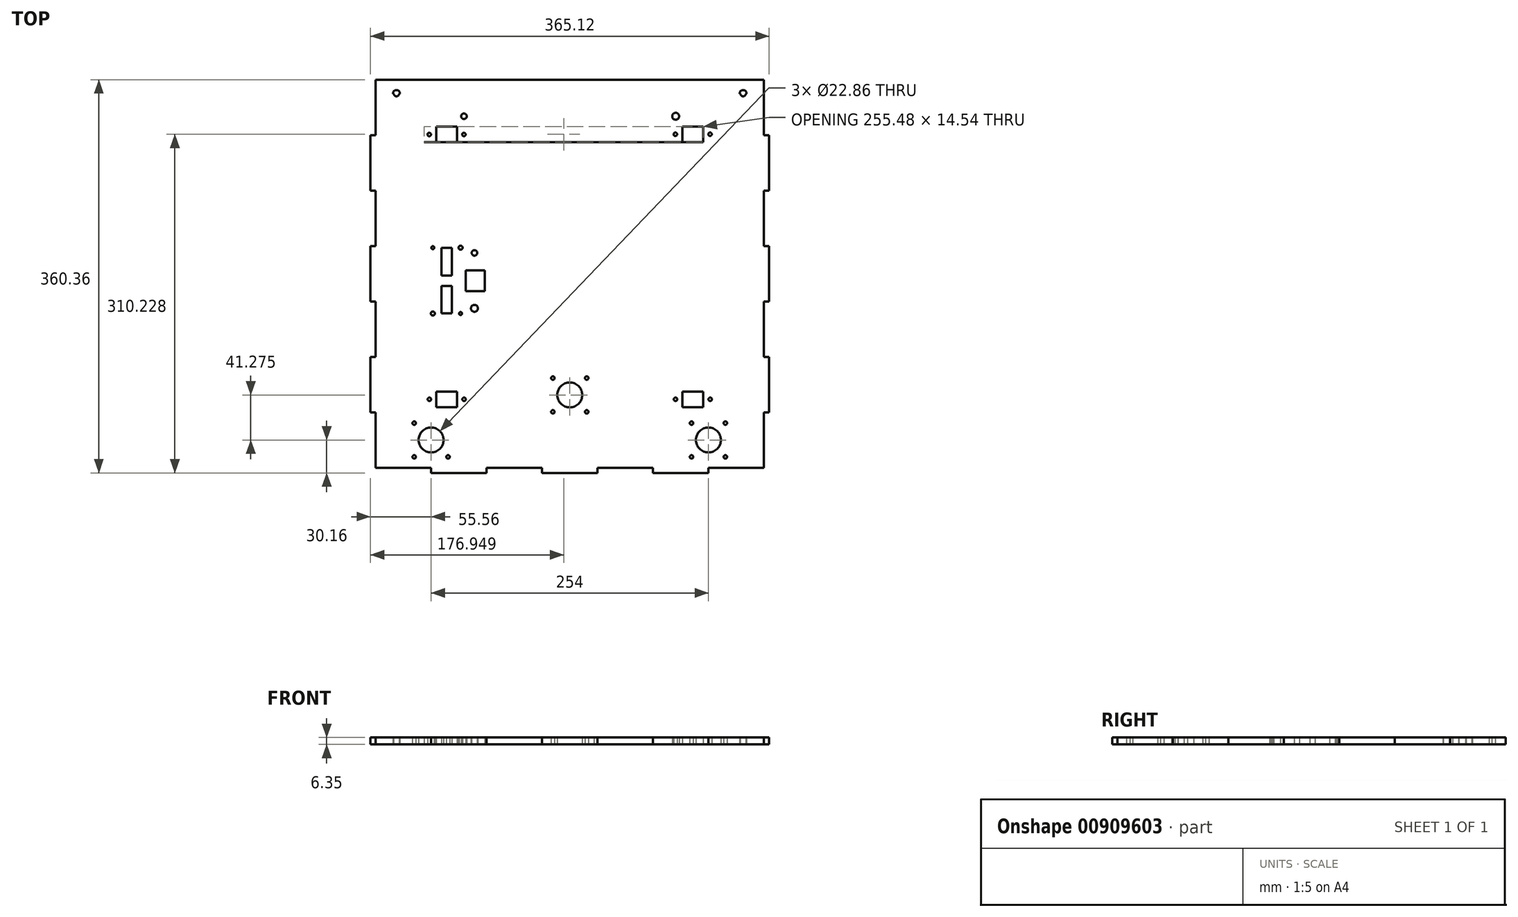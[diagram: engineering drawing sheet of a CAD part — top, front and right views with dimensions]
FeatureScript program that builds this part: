
annotation { "Feature Type Name" : "Feature", "Feature Type Description" : "" }
export const myFeature = defineFeature(function(context is Context, id is Id, definition is map)
    precondition{}
    {
        {
            var Q0;
            Q0=qCreatedBy(makeId("Top.planeOp"),FACE);
            var sketch = newSketch(context, id + "F0", { "sketchPlane" : qUnion([Q0])});
            skLineSegment(sketch, "E0.bottom", {"start": v(-177.8, 171.45) * mm, "end": v(177.8, 171.45) * mm});
            skLineSegment(sketch, "E0.top", {"start": v(-177.8, -171.45) * mm, "end": v(177.8, -171.45) * mm});
            skLineSegment(sketch, "E0.left", {"start": v(-177.8, 171.45) * mm, "end": v(-177.8, -171.45) * mm});
            skLineSegment(sketch, "E0.right", {"start": v(177.8, 171.45) * mm, "end": v(177.8, -171.45) * mm});
            skPoint(sketch, "E0.middle", {"position": v(0, 0) * mm});
            skLineSegment(sketch, "E1.0", {"start": v(-133.35, -101.6) * mm, "end": v(133.35, -101.6) * mm});
            skLineSegment(sketch, "E2.0", {"start": v(-133.35, 127) * mm, "end": v(-133.35, -101.6) * mm});
            skLineSegment(sketch, "E3", {"start": v(0, 171.45) * mm, "end": v(0, -171.45) * mm, "construction": true});
            skLineSegment(sketch, "E4", {"start": v(-177.8, 0) * mm, "end": v(177.8, 0) * mm, "construction": true});
            skLineSegment(sketch, "E5.MirrorCS", {"start": v(133.35, 127) * mm, "end": v(133.35, -101.6) * mm});
            skLineSegment(sketch, "E6.0", {"start": v(-133.35, 127) * mm, "end": v(133.35, 127) * mm});
            skLineSegment(sketch, "E7.bottom", {"start": v(-130.17, 34.93) * mm, "end": v(-95.25, 34.93) * mm});
            skLineSegment(sketch, "E7.top", {"start": v(-130.17, -34.92) * mm, "end": v(-95.25, -34.92) * mm});
            skLineSegment(sketch, "E7.left", {"start": v(-130.18, 34.92) * mm, "end": v(-130.18, -34.92) * mm});
            skLineSegment(sketch, "E7.right", {"start": v(-95.25, 34.92) * mm, "end": v(-95.25, -34.92) * mm});
            skLineSegment(sketch, "E8", {"start": v(-112.71, 34.93) * mm, "end": v(-112.71, -171.45) * mm, "construction": true});
            skLineSegment(sketch, "E9.bottom", {"start": v(-107.95, 4.76) * mm, "end": v(-117.48, 4.76) * mm});
            skLineSegment(sketch, "E9.top", {"start": v(-107.95, 30.04) * mm, "end": v(-117.48, 30.04) * mm});
            skLineSegment(sketch, "E9.left", {"start": v(-107.95, 4.76) * mm, "end": v(-107.95, 30.04) * mm});
            skLineSegment(sketch, "E9.right", {"start": v(-117.48, 4.76) * mm, "end": v(-117.48, 30.04) * mm});
            skPoint(sketch, "E10", {"position": v(-95.25, 0) * mm});
            skLineSegment(sketch, "E11.MirrorCS", {"start": v(-117.48, -4.76) * mm, "end": v(-117.48, -30.04) * mm});
            skLineSegment(sketch, "E12.MirrorCS", {"start": v(-107.95, -4.76) * mm, "end": v(-107.95, -30.04) * mm});
            skPoint(sketch, "E13.MirrorP", {"position": v(-112.71, -12.57) * mm});
            skLineSegment(sketch, "E14.MirrorCS", {"start": v(-107.95, -4.76) * mm, "end": v(-117.48, -4.76) * mm});
            skLineSegment(sketch, "E15.MirrorCS", {"start": v(-107.95, -30.04) * mm, "end": v(-117.48, -30.04) * mm});
            skCircle(sketch, "E16", {"center": v(-127, -146.05) * mm, "radius": 11.43 * mm});
            skCircle(sketch, "E17", {"center": v(-111.5, -130.56) * mm, "radius": 1.59 * mm});
            skCircle(sketch, "E18.1.0", {"center": v(-142.5, -130.56) * mm, "radius": 1.59 * mm});
            skCircle(sketch, "E18.2.0", {"center": v(-142.5, -161.54) * mm, "radius": 1.59 * mm});
            skCircle(sketch, "E18.3.0", {"center": v(-111.5, -161.54) * mm, "radius": 1.59 * mm});
            skCircle(sketch, "E19.MirrorC", {"center": v(142.5, -130.56) * mm, "radius": 1.59 * mm});
            skCircle(sketch, "E20.MirrorC", {"center": v(111.5, -130.56) * mm, "radius": 1.59 * mm});
            skCircle(sketch, "E21.MirrorC", {"center": v(142.5, -161.54) * mm, "radius": 1.59 * mm});
            skPoint(sketch, "E22.MirrorP", {"position": v(127, -146.05) * mm});
            skCircle(sketch, "E23.MirrorC", {"center": v(111.5, -161.54) * mm, "radius": 1.59 * mm});
            skCircle(sketch, "E24.MirrorC", {"center": v(127, -146.05) * mm, "radius": 11.43 * mm});
            skPoint(sketch, "E25.orphan", {"position": v(-112.71, -34.93) * mm});
            skCircle(sketch, "E26", {"center": v(-128.59, -108.75) * mm, "radius": 1.59 * mm});
            skCircle(sketch, "E27.MirrorC", {"center": v(-96.84, -108.75) * mm, "radius": 1.59 * mm});
            skLineSegment(sketch, "E28.bottom", {"start": v(-122.24, -101.6) * mm, "end": v(-103.19, -101.6) * mm});
            skLineSegment(sketch, "E28.top", {"start": v(-122.24, -115.9) * mm, "end": v(-103.19, -115.9) * mm});
            skLineSegment(sketch, "E28.left", {"start": v(-122.24, -101.6) * mm, "end": v(-122.24, -115.9) * mm});
            skLineSegment(sketch, "E28.right", {"start": v(-103.19, -101.6) * mm, "end": v(-103.19, -115.9) * mm});
            skPoint(sketch, "E29", {"position": v(-112.71, -115.9) * mm});
            skLineSegment(sketch, "E30.MirrorCS", {"start": v(122.24, -101.6) * mm, "end": v(122.24, -115.9) * mm});
            skCircle(sketch, "E31.MirrorC", {"center": v(96.84, -108.75) * mm, "radius": 1.59 * mm});
            skCircle(sketch, "E32.MirrorC", {"center": v(128.59, -108.75) * mm, "radius": 1.59 * mm});
            skLineSegment(sketch, "E33.MirrorCS", {"start": v(122.24, -101.6) * mm, "end": v(103.19, -101.6) * mm});
            skPoint(sketch, "E34.MirrorP", {"position": v(112.71, -115.9) * mm});
            skLineSegment(sketch, "E35.MirrorCS", {"start": v(103.19, -101.6) * mm, "end": v(103.19, -115.9) * mm});
            skLineSegment(sketch, "E36.MirrorCS", {"start": v(122.24, -115.9) * mm, "end": v(103.19, -115.9) * mm});
            skCircle(sketch, "E37.MirrorC", {"center": v(-128.7, 133.9) * mm, "radius": 1.59 * mm});
            skLineSegment(sketch, "E38.MirrorCS", {"start": v(-122.36, 141.06) * mm, "end": v(-103.3, 141.07) * mm});
            skLineSegment(sketch, "E39.MirrorCS", {"start": v(-122.35, 126.76) * mm, "end": v(-103.3, 126.77) * mm});
            skCircle(sketch, "E40.MirrorC", {"center": v(128.47, 134.15) * mm, "radius": 1.59 * mm});
            skLineSegment(sketch, "E41.MirrorCS", {"start": v(-122.35, 126.76) * mm, "end": v(-122.36, 141.06) * mm});
            skCircle(sketch, "E42.MirrorC", {"center": v(-96.95, 133.93) * mm, "radius": 1.59 * mm});
            skLineSegment(sketch, "E43.MirrorCS", {"start": v(122.12, 141.29) * mm, "end": v(103.07, 141.27) * mm});
            skCircle(sketch, "E44.MirrorC", {"center": v(96.72, 134.12) * mm, "radius": 1.59 * mm});
            skLineSegment(sketch, "E45.MirrorCS", {"start": v(122.13, 126.99) * mm, "end": v(103.08, 126.97) * mm});
            skPoint(sketch, "E46.MirrorP", {"position": v(-112.83, 141.07) * mm});
            skPoint(sketch, "E47.MirrorP", {"position": v(112.6, 141.28) * mm});
            skLineSegment(sketch, "E48.MirrorCS", {"start": v(-133.46, 126.75) * mm, "end": v(133.24, 127) * mm});
            skLineSegment(sketch, "E49.MirrorCS", {"start": v(103.08, 126.97) * mm, "end": v(103.07, 141.27) * mm});
            skLineSegment(sketch, "E50.MirrorCS", {"start": v(-103.3, 126.77) * mm, "end": v(-103.3, 141.07) * mm});
            skLineSegment(sketch, "E51.MirrorCS", {"start": v(122.13, 126.99) * mm, "end": v(122.12, 141.29) * mm});
            skLineSegment(sketch, "E52.bottom", {"start": v(-95.25, -9.53) * mm, "end": v(-77.79, -9.53) * mm});
            skLineSegment(sketch, "E52.top", {"start": v(-95.25, 9.52) * mm, "end": v(-77.79, 9.52) * mm});
            skLineSegment(sketch, "E52.left", {"start": v(-95.25, -9.53) * mm, "end": v(-95.25, 9.52) * mm});
            skLineSegment(sketch, "E52.right", {"start": v(-77.79, -9.53) * mm, "end": v(-77.79, 9.52) * mm});
            skPoint(sketch, "E53", {"position": v(-65.09, 0) * mm});
            skLineSegment(sketch, "E54.bottom", {"start": v(-95.25, -34.92) * mm, "end": v(-77.79, -34.92) * mm});
            skLineSegment(sketch, "E54.top", {"start": v(-95.25, 34.93) * mm, "end": v(-77.79, 34.93) * mm});
            skLineSegment(sketch, "E54.left", {"start": v(-95.25, -34.92) * mm, "end": v(-95.25, 34.92) * mm});
            skLineSegment(sketch, "E54.right", {"start": v(-77.79, -34.92) * mm, "end": v(-77.79, 34.92) * mm});
            skLineSegment(sketch, "E55.0", {"start": v(-100.01, 34.92) * mm, "end": v(-77.79, 34.92) * mm});
            skLineSegment(sketch, "E55.1", {"start": v(-130.18, 34.92) * mm, "end": v(-100.01, 34.92) * mm});
            skLineSegment(sketch, "E56", {"start": v(-77.79, 34.92) * mm, "end": v(-77.79, 34.92) * mm});
            skLineSegment(sketch, "E57", {"start": v(-130.18, 34.92) * mm, "end": v(-130.18, 34.92) * mm});
            skLineSegment(sketch, "E58.MirrorCS", {"start": v(-130.18, -34.92) * mm, "end": v(-130.18, -34.92) * mm});
            skLineSegment(sketch, "E59.MirrorCS", {"start": v(-100.01, -34.93) * mm, "end": v(-77.79, -34.93) * mm});
            skLineSegment(sketch, "E60.MirrorCS", {"start": v(-130.18, -34.93) * mm, "end": v(-100.01, -34.93) * mm});
            skLineSegment(sketch, "E61.MirrorCS", {"start": v(-77.79, -34.92) * mm, "end": v(-77.79, -34.92) * mm});
            skCircle(sketch, "E62", {"center": v(-87.31, 25.4) * mm, "radius": 3.18 * mm});
            skCircle(sketch, "E63.MirrorC", {"center": v(-87.31, -25.4) * mm, "radius": 3.18 * mm});
            skCircle(sketch, "E64", {"center": v(-125.41, 30.16) * mm, "radius": 1.84 * mm});
            skCircle(sketch, "E65.MirrorC", {"center": v(-100.01, 30.16) * mm, "radius": 1.84 * mm});
            skCircle(sketch, "E66.MirrorC", {"center": v(-125.41, -30.16) * mm, "radius": 1.84 * mm});
            skCircle(sketch, "E67.MirrorC", {"center": v(-100.01, -30.16) * mm, "radius": 1.84 * mm});
            skCircle(sketch, "E68", {"center": v(-158.75, 171.45) * mm, "radius": 3.18 * mm});
            skCircle(sketch, "E69", {"center": v(-96.95, 150.6) * mm, "radius": 3.18 * mm});
            skCircle(sketch, "E70.MirrorC", {"center": v(96.95, 150.6) * mm, "radius": 3.18 * mm});
            skCircle(sketch, "E71.MirrorC", {"center": v(158.75, 171.45) * mm, "radius": 3.18 * mm});
            skLineSegment(sketch, "E72.0", {"start": v(-177.8, 184.15) * mm, "end": v(177.8, 184.15) * mm});
            skLineSegment(sketch, "E73", {"start": v(-177.8, 171.45) * mm, "end": v(-177.8, 184.15) * mm});
            skLineSegment(sketch, "E74", {"start": v(177.8, 171.45) * mm, "end": v(177.8, 184.15) * mm});
            skLineSegment(sketch, "E75.bottom", {"start": v(-177.8, 133.35) * mm, "end": v(-182.56, 133.35) * mm});
            skLineSegment(sketch, "E75.top", {"start": v(-177.8, 82.55) * mm, "end": v(-182.56, 82.55) * mm});
            skLineSegment(sketch, "E75.left", {"start": v(-177.8, 133.35) * mm, "end": v(-177.8, 82.55) * mm});
            skLineSegment(sketch, "E75.right", {"start": v(-182.56, 133.35) * mm, "end": v(-182.56, 82.55) * mm});
            skLineSegment(sketch, "E76.bottom", {"start": v(-177.8, 31.75) * mm, "end": v(-182.56, 31.75) * mm});
            skLineSegment(sketch, "E76.top", {"start": v(-177.8, -19.05) * mm, "end": v(-182.56, -19.05) * mm});
            skLineSegment(sketch, "E76.left", {"start": v(-177.8, 31.75) * mm, "end": v(-177.8, -19.05) * mm});
            skLineSegment(sketch, "E76.right", {"start": v(-182.56, 31.75) * mm, "end": v(-182.56, -19.05) * mm});
            skLineSegment(sketch, "E77.bottom", {"start": v(-177.8, -69.85) * mm, "end": v(-182.56, -69.85) * mm});
            skLineSegment(sketch, "E77.top", {"start": v(-177.8, -120.65) * mm, "end": v(-182.56, -120.65) * mm});
            skLineSegment(sketch, "E77.left", {"start": v(-177.8, -69.85) * mm, "end": v(-177.8, -120.65) * mm});
            skLineSegment(sketch, "E77.right", {"start": v(-182.56, -69.85) * mm, "end": v(-182.56, -120.65) * mm});
            skLineSegment(sketch, "E78.MirrorCS", {"start": v(177.8, -120.65) * mm, "end": v(182.56, -120.65) * mm});
            skLineSegment(sketch, "E79.MirrorCS", {"start": v(177.8, 31.75) * mm, "end": v(182.56, 31.75) * mm});
            skLineSegment(sketch, "E80.MirrorCS", {"start": v(177.8, -19.05) * mm, "end": v(182.56, -19.05) * mm});
            skLineSegment(sketch, "E81.MirrorCS", {"start": v(177.8, 82.55) * mm, "end": v(182.56, 82.55) * mm});
            skLineSegment(sketch, "E82.MirrorCS", {"start": v(177.8, -69.85) * mm, "end": v(182.56, -69.85) * mm});
            skLineSegment(sketch, "E83.MirrorCS", {"start": v(177.8, 133.35) * mm, "end": v(182.56, 133.35) * mm});
            skLineSegment(sketch, "E84.MirrorCS", {"start": v(182.56, 133.35) * mm, "end": v(182.56, 82.55) * mm});
            skLineSegment(sketch, "E85.MirrorCS", {"start": v(177.8, 31.75) * mm, "end": v(177.8, -19.05) * mm});
            skLineSegment(sketch, "E86.MirrorCS", {"start": v(182.56, 31.75) * mm, "end": v(182.56, -19.05) * mm});
            skLineSegment(sketch, "E87.MirrorCS", {"start": v(177.8, 133.35) * mm, "end": v(177.8, 82.55) * mm});
            skLineSegment(sketch, "E88.MirrorCS", {"start": v(177.8, -69.85) * mm, "end": v(177.8, -120.65) * mm});
            skLineSegment(sketch, "E89.MirrorCS", {"start": v(182.56, -69.85) * mm, "end": v(182.56, -120.65) * mm});
            skLineSegment(sketch, "E90.bottom", {"start": v(-127, 184.15) * mm, "end": v(-76.2, 184.15) * mm});
            skLineSegment(sketch, "E90.top", {"start": v(-127, 188.91) * mm, "end": v(-76.2, 188.91) * mm});
            skLineSegment(sketch, "E90.left", {"start": v(-127, 184.15) * mm, "end": v(-127, 188.91) * mm});
            skLineSegment(sketch, "E90.right", {"start": v(-76.2, 184.15) * mm, "end": v(-76.2, 188.91) * mm});
            skLineSegment(sketch, "E91.bottom", {"start": v(-25.4, 184.15) * mm, "end": v(25.4, 184.15) * mm});
            skLineSegment(sketch, "E91.top", {"start": v(-25.4, 188.91) * mm, "end": v(25.4, 188.91) * mm});
            skLineSegment(sketch, "E91.left", {"start": v(-25.4, 184.15) * mm, "end": v(-25.4, 188.91) * mm});
            skLineSegment(sketch, "E91.right", {"start": v(25.4, 184.15) * mm, "end": v(25.4, 188.91) * mm});
            skLineSegment(sketch, "E92.bottom", {"start": v(76.2, 184.15) * mm, "end": v(127, 184.15) * mm});
            skLineSegment(sketch, "E92.top", {"start": v(76.2, 188.91) * mm, "end": v(127, 188.91) * mm});
            skLineSegment(sketch, "E92.left", {"start": v(76.2, 184.15) * mm, "end": v(76.2, 188.91) * mm});
            skLineSegment(sketch, "E92.right", {"start": v(127, 184.15) * mm, "end": v(127, 188.91) * mm});
            skLineSegment(sketch, "E93", {"start": v(177.8, 184.15) * mm, "end": v(177.8, -171.45) * mm, "construction": true});
            skLineSegment(sketch, "E94", {"start": v(177.8, 6.35) * mm, "end": v(-210.69, 6.35) * mm, "construction": true});
            skLineSegment(sketch, "E95.MirrorCS", {"start": v(25.4, -171.45) * mm, "end": v(25.4, -176.21) * mm});
            skLineSegment(sketch, "E96.MirrorCS", {"start": v(76.2, -171.45) * mm, "end": v(76.2, -176.21) * mm});
            skLineSegment(sketch, "E97.MirrorCS", {"start": v(127, -171.45) * mm, "end": v(127, -176.21) * mm});
            skLineSegment(sketch, "E98.MirrorCS", {"start": v(-127, -171.45) * mm, "end": v(-127, -176.21) * mm});
            skLineSegment(sketch, "E99.MirrorCS", {"start": v(-25.4, -171.45) * mm, "end": v(-25.4, -176.21) * mm});
            skLineSegment(sketch, "E100.MirrorCS", {"start": v(-76.2, -171.45) * mm, "end": v(-76.2, -176.21) * mm});
            skLineSegment(sketch, "E101.MirrorCS", {"start": v(76.2, -171.45) * mm, "end": v(127, -171.45) * mm});
            skLineSegment(sketch, "E102.MirrorCS", {"start": v(-127, -176.21) * mm, "end": v(-76.2, -176.21) * mm});
            skLineSegment(sketch, "E103.MirrorCS", {"start": v(76.2, -176.21) * mm, "end": v(127, -176.21) * mm});
            skLineSegment(sketch, "E104.MirrorCS", {"start": v(-25.4, -171.45) * mm, "end": v(25.4, -171.45) * mm});
            skLineSegment(sketch, "E105.MirrorCS", {"start": v(-25.4, -176.21) * mm, "end": v(25.4, -176.21) * mm});
            skLineSegment(sketch, "E106.MirrorCS", {"start": v(-127, -171.45) * mm, "end": v(-76.2, -171.45) * mm});
            skLineSegment(sketch, "E107.bottom", {"start": v(-22.23, 126.85) * mm, "end": v(22.22, 126.85) * mm});
            skLineSegment(sketch, "E107.top", {"start": v(-22.23, 168.13) * mm, "end": v(22.22, 168.13) * mm});
            skLineSegment(sketch, "E107.left", {"start": v(-22.23, 126.85) * mm, "end": v(-22.23, 168.13) * mm});
            skLineSegment(sketch, "E107.right", {"start": v(22.22, 126.85) * mm, "end": v(22.22, 168.13) * mm});
            skPoint(sketch, "E108", {"position": v(0, 168.13) * mm});
            skCircle(sketch, "E109", {"center": v(0, -104.77) * mm, "radius": 11.43 * mm});
            skLineSegment(sketch, "E110.bottom", {"start": v(20.64, -84.14) * mm, "end": v(-20.64, -84.14) * mm});
            skLineSegment(sketch, "E110.top", {"start": v(20.64, -125.41) * mm, "end": v(-20.64, -125.41) * mm});
            skLineSegment(sketch, "E110.left", {"start": v(20.64, -84.14) * mm, "end": v(20.64, -125.41) * mm});
            skLineSegment(sketch, "E110.right", {"start": v(-20.64, -84.14) * mm, "end": v(-20.64, -125.41) * mm});
            skCircle(sketch, "E111", {"center": v(-15.5, -120.27) * mm, "radius": 1.59 * mm});
            skCircle(sketch, "E112.1.0", {"center": v(15.5, -120.27) * mm, "radius": 1.59 * mm});
            skCircle(sketch, "E112.2.0", {"center": v(15.5, -89.28) * mm, "radius": 1.59 * mm});
            skCircle(sketch, "E113.1.3.0", {"center": v(-15.5, -89.28) * mm, "radius": 1.59 * mm});
            skSolve(sketch);
        }
        {
            var Q0;
            Q0=makeQuery(id+"F0.imprint","IMPRINT",FACE,{"disambiguationData":[TD([[makeQuery(id+"F0.imprint","IMPRINT",EDGE,{"derivedFrom":sQuery(id+"F0.wireOp",EDGE,"E0.bottom")}),-1.0]])]});
            var Q1;
            {var subQ0=sQuery(id+"F0.wireOp",EDGE,"E7.bottom");Q1=makeQuery(id+"F0.imprint","IMPRINT",FACE,{"disambiguationData":[TD([[makeQuery(id+"F0.imprint","IMPRINT",EDGE,{"derivedFrom":subQ0}),-1.0]])]});}
            var Q2;
            {var subQ1=sQuery(id+"F0.wireOp",EDGE,"E52.bottom");Q2=makeQuery(id+"F0.imprint","IMPRINT",FACE,{"disambiguationData":[TD([[makeQuery(id+"F0.imprint","IMPRINT",EDGE,{"derivedFrom":subQ1}),-1.0]])]});}
            var Q3;
            {var subQ7=sQuery(id+"F0.wireOp",EDGE,"E52.top");Q3=makeQuery(id+"F0.imprint","IMPRINT",FACE,{"disambiguationData":[TD([[makeQuery(id+"F0.imprint","IMPRINT",EDGE,{"derivedFrom":subQ7}),1.0]])]});}
            var Q4;
            {var subQ0=sQuery(id+"F0.wireOp",EDGE,"E7.top");Q4=makeQuery(id+"F0.imprint","IMPRINT",FACE,{"disambiguationData":[TD([[makeQuery(id+"F0.imprint","IMPRINT",EDGE,{"derivedFrom":subQ0}),-1.0]])]});}
            var Q5;
            {var subQ1=sQuery(id+"F0.wireOp",EDGE,"E7.bottom");Q5=makeQuery(id+"F0.imprint","IMPRINT",FACE,{"disambiguationData":[TD([[makeQuery(id+"F0.imprint","IMPRINT",EDGE,{"derivedFrom":subQ1}),1.0]])]});}
            var Q6;
            {var subQ0=sQuery(id+"F0.wireOp",EDGE,"E62");var subQ1=sQuery(id+"F0.wireOp",EDGE,"E54.top");var subQ2=makeQuery(id+"F0.imprint","INTERSECT",VERTEX,{"disambiguationData":[OD(0.0)],"derivedFrom":[subQ1,subQ0]});Q6=makeQuery(id+"F0.imprint","IMPRINT",FACE,{"disambiguationData":[TD([[makeQuery(id+"F0.imprint","IMPRINT",EDGE,{"disambiguationData":[TD([[subQ2,-1.0]])],"derivedFrom":subQ1}),-1.0]])]});}
            var Q7;
            Q7=makeQuery(id+"F0.imprint","IMPRINT",FACE,{"disambiguationData":[TD([[makeQuery(id+"F0.imprint","IMPRINT",EDGE,{"derivedFrom":sQuery(id+"F0.wireOp",EDGE,"E65.MirrorC")}),-1.0]])]});
            var Q8;
            Q8=makeQuery(id+"F0.imprint","IMPRINT",FACE,{"disambiguationData":[TD([[makeQuery(id+"F0.imprint","IMPRINT",EDGE,{"derivedFrom":sQuery(id+"F0.wireOp",EDGE,"E64")}),1.0]])]});
            var Q9;
            Q9=makeQuery(id+"F0.imprint","IMPRINT",FACE,{"disambiguationData":[TD([[makeQuery(id+"F0.imprint","IMPRINT",EDGE,{"derivedFrom":sQuery(id+"F0.wireOp",EDGE,"E66.MirrorC")}),-1.0]])]});
            var Q10;
            {var subQ0=sQuery(id+"F0.wireOp",EDGE,"E62");var subQ1=sQuery(id+"F0.wireOp",EDGE,"E54.top");var subQ2=makeQuery(id+"F0.imprint","INTERSECT",VERTEX,{"disambiguationData":[OD(0.0)],"derivedFrom":[subQ1,subQ0]});Q10=makeQuery(id+"F0.imprint","IMPRINT",FACE,{"disambiguationData":[TD([[makeQuery(id+"F0.imprint","IMPRINT",EDGE,{"disambiguationData":[TD([[subQ2,-1.0]])],"derivedFrom":subQ1}),1.0]])]});}
            var Q11;
            Q11=makeQuery(id+"F0.imprint","IMPRINT",FACE,{"disambiguationData":[TD([[makeQuery(id+"F0.imprint","IMPRINT",EDGE,{"derivedFrom":sQuery(id+"F0.wireOp",EDGE,"E67.MirrorC")}),1.0]])]});
            var Q12;
            {var subQ0=sQuery(id+"F0.wireOp",EDGE,"E63.MirrorC");var subQ1=sQuery(id+"F0.wireOp",EDGE,"E54.bottom");var subQ2=makeQuery(id+"F0.imprint","INTERSECT",VERTEX,{"disambiguationData":[OD(0.0)],"derivedFrom":[subQ1,subQ0]});Q12=makeQuery(id+"F0.imprint","IMPRINT",FACE,{"disambiguationData":[TD([[makeQuery(id+"F0.imprint","IMPRINT",EDGE,{"disambiguationData":[TD([[subQ2,-1.0]])],"derivedFrom":subQ1}),1.0]])]});}
            var Q13;
            Q13=makeQuery(id+"F0.imprint","IMPRINT",FACE,{"disambiguationData":[TD([[makeQuery(id+"F0.imprint","IMPRINT",EDGE,{"derivedFrom":sQuery(id+"F0.wireOp",EDGE,"E0.top")}),1.0]])]});
            var Q14;
            Q14=makeQuery(id+"F0.imprint","IMPRINT",FACE,{"disambiguationData":[TD([[makeQuery(id+"F0.imprint","IMPRINT",EDGE,{"derivedFrom":sQuery(id+"F0.wireOp",EDGE,"E72.0")}),-1.0]])]});
            var Q15;
            {var subQ0=sQuery(id+"F0.wireOp",EDGE,"E68");var subQ1=sQuery(id+"F0.wireOp",EDGE,"E0.bottom");var subQ2=makeQuery(id+"F0.imprint","INTERSECT",VERTEX,{"disambiguationData":[OD(0.0)],"derivedFrom":[subQ1,subQ0]});Q15=makeQuery(id+"F0.imprint","IMPRINT",FACE,{"disambiguationData":[TD([[makeQuery(id+"F0.imprint","IMPRINT",EDGE,{"disambiguationData":[TD([[subQ2,-1.0]])],"derivedFrom":subQ1}),1.0]])]});}
            var Q16;
            {var subQ0=sQuery(id+"F0.wireOp",EDGE,"E71.MirrorC");var subQ1=sQuery(id+"F0.wireOp",EDGE,"E0.bottom");var subQ2=makeQuery(id+"F0.imprint","INTERSECT",VERTEX,{"disambiguationData":[OD(0.0)],"derivedFrom":[subQ1,subQ0]});Q16=makeQuery(id+"F0.imprint","IMPRINT",FACE,{"disambiguationData":[TD([[makeQuery(id+"F0.imprint","IMPRINT",EDGE,{"disambiguationData":[TD([[subQ2,-1.0]])],"derivedFrom":subQ1}),1.0]])]});}
            var Q17;
            Q17=makeQuery(id+"F0.imprint","IMPRINT",FACE,{"disambiguationData":[TD([[makeQuery(id+"F0.imprint","IMPRINT",EDGE,{"derivedFrom":sQuery(id+"F0.wireOp",EDGE,"E69")}),1.0]])]});
            var Q18;
            Q18=makeQuery(id+"F0.imprint","IMPRINT",FACE,{"disambiguationData":[TD([[makeQuery(id+"F0.imprint","IMPRINT",EDGE,{"derivedFrom":sQuery(id+"F0.wireOp",EDGE,"E70.MirrorC")}),-1.0]])]});
            var Q19;
            Q19=makeQuery(id+"F0.imprint","IMPRINT",FACE,{"disambiguationData":[TD([[makeQuery(id+"F0.imprint","IMPRINT",EDGE,{"derivedFrom":sQuery(id+"F0.wireOp",EDGE,"E75.bottom")}),1.0]])]});
            var Q20;
            Q20=makeQuery(id+"F0.imprint","IMPRINT",FACE,{"disambiguationData":[TD([[makeQuery(id+"F0.imprint","IMPRINT",EDGE,{"derivedFrom":sQuery(id+"F0.wireOp",EDGE,"E90.bottom")}),1.0]])]});
            var Q21;
            Q21=makeQuery(id+"F0.imprint","IMPRINT",FACE,{"disambiguationData":[TD([[makeQuery(id+"F0.imprint","IMPRINT",EDGE,{"derivedFrom":sQuery(id+"F0.wireOp",EDGE,"E91.bottom")}),1.0]])]});
            var Q22;
            Q22=makeQuery(id+"F0.imprint","IMPRINT",FACE,{"disambiguationData":[TD([[makeQuery(id+"F0.imprint","IMPRINT",EDGE,{"derivedFrom":sQuery(id+"F0.wireOp",EDGE,"E92.bottom")}),1.0]])]});
            var Q23;
            Q23=makeQuery(id+"F0.imprint","IMPRINT",FACE,{"disambiguationData":[TD([[makeQuery(id+"F0.imprint","IMPRINT",EDGE,{"derivedFrom":sQuery(id+"F0.wireOp",EDGE,"E81.MirrorCS")}),1.0]])]});
            var Q24;
            Q24=makeQuery(id+"F0.imprint","IMPRINT",FACE,{"disambiguationData":[TD([[makeQuery(id+"F0.imprint","IMPRINT",EDGE,{"derivedFrom":sQuery(id+"F0.wireOp",EDGE,"E79.MirrorCS")}),-1.0]])]});
            var Q25;
            Q25=makeQuery(id+"F0.imprint","IMPRINT",FACE,{"disambiguationData":[TD([[makeQuery(id+"F0.imprint","IMPRINT",EDGE,{"derivedFrom":sQuery(id+"F0.wireOp",EDGE,"E78.MirrorCS")}),1.0]])]});
            var Q26;
            Q26=makeQuery(id+"F0.imprint","IMPRINT",FACE,{"disambiguationData":[TD([[makeQuery(id+"F0.imprint","IMPRINT",EDGE,{"derivedFrom":sQuery(id+"F0.wireOp",EDGE,"E77.bottom")}),1.0]])]});
            var Q27;
            Q27=makeQuery(id+"F0.imprint","IMPRINT",FACE,{"disambiguationData":[TD([[makeQuery(id+"F0.imprint","IMPRINT",EDGE,{"derivedFrom":sQuery(id+"F0.wireOp",EDGE,"E76.bottom")}),1.0]])]});
            var Q28;
            Q28=makeQuery(id+"F0.imprint","IMPRINT",FACE,{"disambiguationData":[TD([[makeQuery(id+"F0.imprint","IMPRINT",EDGE,{"derivedFrom":sQuery(id+"F0.wireOp",EDGE,"E98.MirrorCS")}),1.0]])]});
            var Q29;
            Q29=makeQuery(id+"F0.imprint","IMPRINT",FACE,{"disambiguationData":[TD([[makeQuery(id+"F0.imprint","IMPRINT",EDGE,{"derivedFrom":sQuery(id+"F0.wireOp",EDGE,"E95.MirrorCS")}),-1.0]])]});
            var Q30;
            Q30=makeQuery(id+"F0.imprint","IMPRINT",FACE,{"disambiguationData":[TD([[makeQuery(id+"F0.imprint","IMPRINT",EDGE,{"derivedFrom":sQuery(id+"F0.wireOp",EDGE,"E96.MirrorCS")}),1.0]])]});
            var Q31;
            {var subQ5=sQuery(id+"F0.wireOp",EDGE,"E107.top");Q31=makeQuery(id+"F0.imprint","IMPRINT",FACE,{"disambiguationData":[TD([[makeQuery(id+"F0.imprint","IMPRINT",EDGE,{"derivedFrom":subQ5}),-1.0]])]});}
            var Q32;
            Q32=makeQuery(id+"F0.imprint","IMPRINT",FACE,{"disambiguationData":[TD([[makeQuery(id+"F0.imprint","IMPRINT",EDGE,{"derivedFrom":sQuery(id+"F0.wireOp",EDGE,"E7.left")}),1.0]])]});
            var Q33;
            Q33=makeQuery(id+"F0.imprint","IMPRINT",FACE,{"disambiguationData":[TD([[makeQuery(id+"F0.imprint","IMPRINT",EDGE,{"derivedFrom":sQuery(id+"F0.wireOp",EDGE,"E62")}),1.0]])]});
            var Q34;
            Q34=makeQuery(id+"F0.imprint","IMPRINT",FACE,{"disambiguationData":[TD([[makeQuery(id+"F0.imprint","IMPRINT",EDGE,{"derivedFrom":sQuery(id+"F0.wireOp",EDGE,"E63.MirrorC")}),-1.0]])]});
            var Q35;
            {var subQ0=sQuery(id+"F0.wireOp",EDGE,"E110.top");Q35=makeQuery(id+"F0.imprint","IMPRINT",FACE,{"disambiguationData":[TD([[makeQuery(id+"F0.imprint","IMPRINT",EDGE,{"derivedFrom":subQ0}),-1.0]])]});}
            var Q36;
            {var subQ0=sQuery(id+"F0.wireOp",EDGE,"E110.bottom");Q36=makeQuery(id+"F0.imprint","IMPRINT",FACE,{"disambiguationData":[TD([[makeQuery(id+"F0.imprint","IMPRINT",EDGE,{"derivedFrom":subQ0}),1.0]])]});}
            extrude(context, id + "F1", {"entities" : qUnion([Q0, Q1, Q2, Q3, Q4, Q5, Q6, Q7, Q8, Q9, Q10, Q11, Q12, Q13, Q14, Q15, Q16, Q17, Q18, Q19, Q20, Q21, Q22, Q23, Q24, Q25, Q26, Q27, Q28, Q29, Q30, Q31, Q32, Q33, Q34, Q35, Q36]), "depth" : 6.35 * mm, "offsetDistance" : 25.4 * mm});
        }
        {
            var Q0;
            Q0=sQuery(id+"F0.wireOp",VERTEX,"E64.center");
            var Q1;
            Q1=sQuery(id+"F0.wireOp",VERTEX,"E65.MirrorC.center");
            var Q2;
            Q2=sQuery(id+"F0.wireOp",VERTEX,"E67.MirrorC.center");
            var Q3;
            Q3=sQuery(id+"F0.wireOp",VERTEX,"E66.MirrorC.center");
            var Q4;
            Q4=makeQuery(id+"F1.opExtrude","SWEPT_BODY",BODY,{"disambiguationData":[OSD([sQuery(id+"F0.wireOp",EDGE,"E7.left"),sQuery(id+"F0.wireOp",EDGE,"E9.bottom"),sQuery(id+"F0.wireOp",EDGE,"E9.top"),sQuery(id+"F0.wireOp",EDGE,"E9.left"),sQuery(id+"F0.wireOp",EDGE,"E9.right"),sQuery(id+"F0.wireOp",EDGE,"E11.MirrorCS"),sQuery(id+"F0.wireOp",EDGE,"E12.MirrorCS"),sQuery(id+"F0.wireOp",EDGE,"E14.MirrorCS"),sQuery(id+"F0.wireOp",EDGE,"E15.MirrorCS"),sQuery(id+"F0.wireOp",EDGE,"E52.bottom"),sQuery(id+"F0.wireOp",EDGE,"E52.top"),sQuery(id+"F0.wireOp",EDGE,"E54.left"),sQuery(id+"F0.wireOp",EDGE,"E54.right"),sQuery(id+"F0.wireOp",EDGE,"E55.0"),sQuery(id+"F0.wireOp",EDGE,"E55.1"),sQuery(id+"F0.wireOp",EDGE,"E56"),sQuery(id+"F0.wireOp",EDGE,"E57"),sQuery(id+"F0.wireOp",EDGE,"E58.MirrorCS"),sQuery(id+"F0.wireOp",EDGE,"E59.MirrorCS"),sQuery(id+"F0.wireOp",EDGE,"E60.MirrorCS"),sQuery(id+"F0.wireOp",EDGE,"E61.MirrorCS")])]});
            hole(context, id + "F2", {"style" : HoleStyle.SIMPLE, "endStyle" : HoleEndStyle.THROUGH, "oppositeDirection" : true, "standardTappedOrClearance" : lookupTablePath({ "standard" : "ANSI", "engagement" : "75%", "pitch" : "32 tpi", "size" : "#6", "type" : "Tapped" }), "standardBlindInLast" : lookupTablePath({ "standard" : "ANSI", "engagement" : "75%", "pitch" : "32 tpi", "size" : "#6", "type" : "Tapped" }), "holeDiameter" : 2.7 * mm, "majorDiameter" : 3.5 * mm, "showTappedDepth" : true, "isTappedThrough" : true, "tappedDepth" : 12.7 * mm, "tapClearance" : 3, "locations" : qUnion([Q0, Q1, Q2, Q3]), "scope" : qUnion([Q4])});
        }
        {
            var Q0;
            Q0=sQuery(id+"F0.wireOp",VERTEX,"E62.center");
            var Q1;
            Q1=sQuery(id+"F0.wireOp",VERTEX,"E63.MirrorC.center");
            var Q2;
            Q2=makeQuery(id+"F1.opExtrude","SWEPT_BODY",BODY,{"disambiguationData":[OSD([sQuery(id+"F0.wireOp",EDGE,"E7.left"),sQuery(id+"F0.wireOp",EDGE,"E9.bottom"),sQuery(id+"F0.wireOp",EDGE,"E9.top"),sQuery(id+"F0.wireOp",EDGE,"E9.left"),sQuery(id+"F0.wireOp",EDGE,"E9.right"),sQuery(id+"F0.wireOp",EDGE,"E11.MirrorCS"),sQuery(id+"F0.wireOp",EDGE,"E12.MirrorCS"),sQuery(id+"F0.wireOp",EDGE,"E14.MirrorCS"),sQuery(id+"F0.wireOp",EDGE,"E15.MirrorCS"),sQuery(id+"F0.wireOp",EDGE,"E52.bottom"),sQuery(id+"F0.wireOp",EDGE,"E52.top"),sQuery(id+"F0.wireOp",EDGE,"E54.left"),sQuery(id+"F0.wireOp",EDGE,"E54.right"),sQuery(id+"F0.wireOp",EDGE,"E55.0"),sQuery(id+"F0.wireOp",EDGE,"E55.1"),sQuery(id+"F0.wireOp",EDGE,"E56"),sQuery(id+"F0.wireOp",EDGE,"E57"),sQuery(id+"F0.wireOp",EDGE,"E58.MirrorCS"),sQuery(id+"F0.wireOp",EDGE,"E59.MirrorCS"),sQuery(id+"F0.wireOp",EDGE,"E60.MirrorCS"),sQuery(id+"F0.wireOp",EDGE,"E61.MirrorCS")])]});
            hole(context, id + "F3", {"style" : HoleStyle.SIMPLE, "endStyle" : HoleEndStyle.THROUGH, "oppositeDirection" : true, "standardTappedOrClearance" : lookupTablePath({ "standard" : "ANSI", "engagement" : "75%", "pitch" : "20 tpi", "size" : "1/4", "type" : "Tapped" }), "standardBlindInLast" : lookupTablePath({ "standard" : "ANSI", "engagement" : "75%", "pitch" : "20 tpi", "size" : "1/4", "type" : "Tapped" }), "holeDiameter" : 5.1 * mm, "majorDiameter" : 6.35 * mm, "showTappedDepth" : true, "isTappedThrough" : true, "tappedDepth" : 12.7 * mm, "tapClearance" : 3, "locations" : qUnion([Q0, Q1]), "scope" : qUnion([Q2])});
        }
        {
            var Q0;
            Q0=sQuery(id+"F0.wireOp",VERTEX,"E68.center");
            var Q1;
            Q1=sQuery(id+"F0.wireOp",VERTEX,"E69.center");
            var Q2;
            Q2=sQuery(id+"F0.wireOp",VERTEX,"E70.MirrorC.center");
            var Q3;
            Q3=sQuery(id+"F0.wireOp",VERTEX,"E71.MirrorC.center");
            var Q4;
            Q4=makeQuery(id+"F1.opExtrude","SWEPT_BODY",BODY,{"disambiguationData":[OSD([sQuery(id+"F0.wireOp",EDGE,"E0.top"),sQuery(id+"F0.wireOp",EDGE,"E0.left"),sQuery(id+"F0.wireOp",EDGE,"E0.right"),sQuery(id+"F0.wireOp",EDGE,"E1.0"),sQuery(id+"F0.wireOp",EDGE,"E2.0"),sQuery(id+"F0.wireOp",EDGE,"E5.MirrorCS"),sQuery(id+"F0.wireOp",EDGE,"E6.0"),sQuery(id+"F0.wireOp",EDGE,"E16"),sQuery(id+"F0.wireOp",EDGE,"E17"),sQuery(id+"F0.wireOp",EDGE,"E18.1.0"),sQuery(id+"F0.wireOp",EDGE,"E18.2.0"),sQuery(id+"F0.wireOp",EDGE,"E18.3.0"),sQuery(id+"F0.wireOp",EDGE,"E19.MirrorC"),sQuery(id+"F0.wireOp",EDGE,"E20.MirrorC"),sQuery(id+"F0.wireOp",EDGE,"E21.MirrorC"),sQuery(id+"F0.wireOp",EDGE,"E23.MirrorC"),sQuery(id+"F0.wireOp",EDGE,"E24.MirrorC"),sQuery(id+"F0.wireOp",EDGE,"E26"),sQuery(id+"F0.wireOp",EDGE,"E27.MirrorC"),sQuery(id+"F0.wireOp",EDGE,"E28.top"),sQuery(id+"F0.wireOp",EDGE,"E28.left"),sQuery(id+"F0.wireOp",EDGE,"E28.right"),sQuery(id+"F0.wireOp",EDGE,"E30.MirrorCS"),sQuery(id+"F0.wireOp",EDGE,"E31.MirrorC"),sQuery(id+"F0.wireOp",EDGE,"E32.MirrorC"),sQuery(id+"F0.wireOp",EDGE,"E35.MirrorCS"),sQuery(id+"F0.wireOp",EDGE,"E36.MirrorCS"),sQuery(id+"F0.wireOp",EDGE,"E37.MirrorC"),sQuery(id+"F0.wireOp",EDGE,"E38.MirrorCS"),sQuery(id+"F0.wireOp",EDGE,"E40.MirrorC"),sQuery(id+"F0.wireOp",EDGE,"E41.MirrorCS"),sQuery(id+"F0.wireOp",EDGE,"E42.MirrorC"),sQuery(id+"F0.wireOp",EDGE,"E43.MirrorCS"),sQuery(id+"F0.wireOp",EDGE,"E44.MirrorC"),sQuery(id+"F0.wireOp",EDGE,"E49.MirrorCS"),sQuery(id+"F0.wireOp",EDGE,"E50.MirrorCS"),sQuery(id+"F0.wireOp",EDGE,"E51.MirrorCS"),sQuery(id+"F0.wireOp",EDGE,"E72.0"),sQuery(id+"F0.wireOp",EDGE,"E73"),sQuery(id+"F0.wireOp",EDGE,"E74")])]});
            hole(context, id + "F4", {"style" : HoleStyle.SIMPLE, "endStyle" : HoleEndStyle.THROUGH, "oppositeDirection" : true, "standardTappedOrClearance" : lookupTablePath({ "standard" : "ANSI", "engagement" : "75%", "pitch" : "20 tpi", "size" : "1/4", "type" : "Tapped" }), "standardBlindInLast" : lookupTablePath({ "standard" : "ANSI", "engagement" : "75%", "pitch" : "20 tpi", "size" : "1/4", "type" : "Tapped" }), "holeDiameter" : 5.1 * mm, "majorDiameter" : 6.35 * mm, "showTappedDepth" : true, "isTappedThrough" : true, "tappedDepth" : 12.7 * mm, "tapClearance" : 3, "locations" : qUnion([Q0, Q1, Q2, Q3]), "scope" : qUnion([Q4])});
        }
    });
